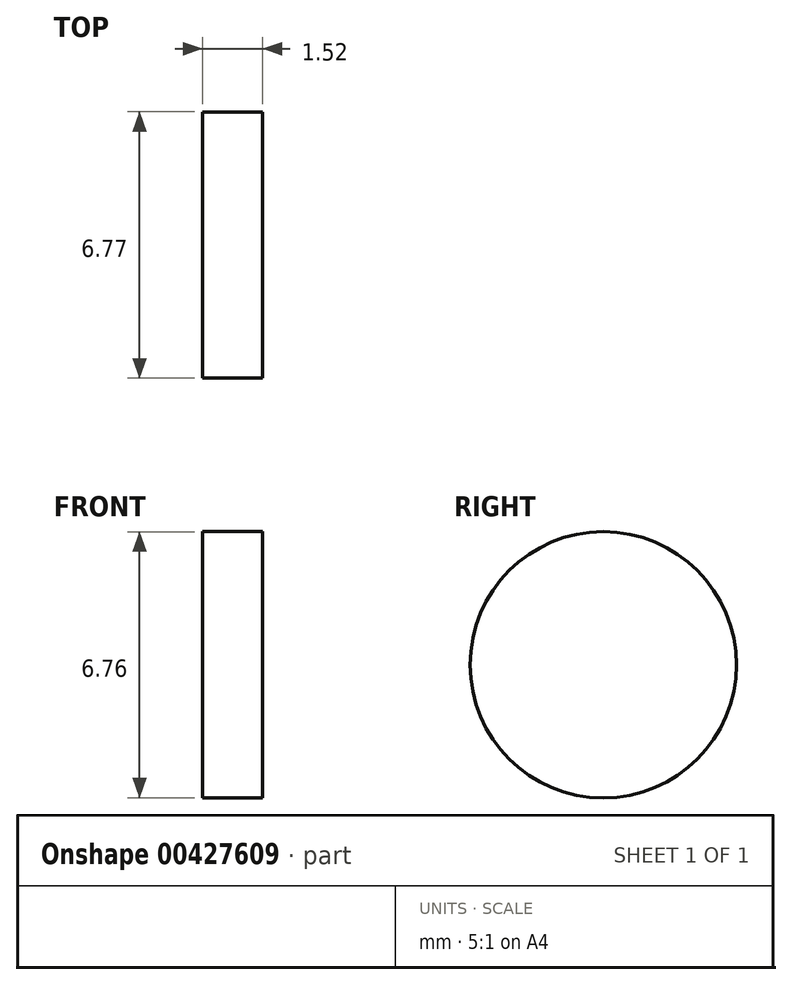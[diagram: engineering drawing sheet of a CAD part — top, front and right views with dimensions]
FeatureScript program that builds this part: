
annotation { "Feature Type Name" : "Feature", "Feature Type Description" : "" }
export const myFeature = defineFeature(function(context is Context, id is Id, definition is map)
    precondition{}
    {
        {
            var Q0;
            Q0=qCreatedBy(makeId("Right.planeOp"),FACE);
            var sketch = newSketch(context, id + "F0", { "sketchPlane" : qUnion([Q0])});
            skCircle(sketch, "E0", {"center": v(-20.12, 18.1) * mm, "radius": 3.38 * mm});
            skSolve(sketch);
        }
        {
            var Q0;
            Q0=makeQuery(id+"F0.imprint","IMPRINT",FACE,{"disambiguationData":[TD([[makeQuery(id+"F0.imprint","IMPRINT",EDGE,{"derivedFrom":sQuery(id+"F0.wireOp",EDGE,"E0")}),1.0]])]});
            extrude(context, id + "F1", {"entities" : qUnion([Q0]), "depth" : 1.52 * mm});
        }
    });
